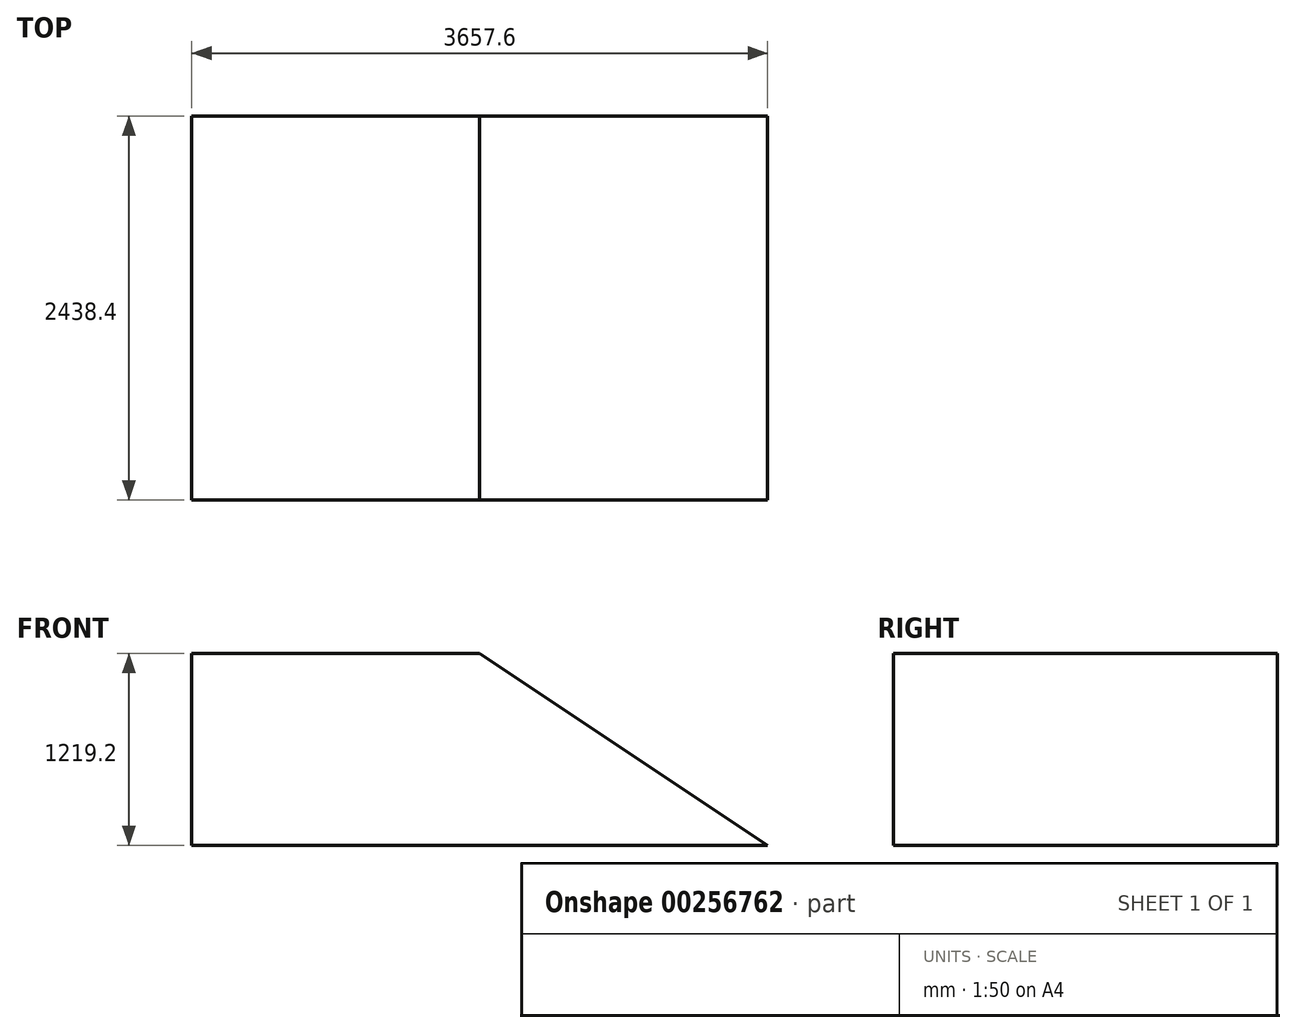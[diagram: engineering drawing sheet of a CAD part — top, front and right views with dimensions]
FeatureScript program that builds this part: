
annotation { "Feature Type Name" : "Feature", "Feature Type Description" : "" }
export const myFeature = defineFeature(function(context is Context, id is Id, definition is map)
    precondition{}
    {
        {
            var Q0;
            Q0=qCreatedBy(makeId("Front.planeOp"),FACE);
            var sketch = newSketch(context, id + "F0", { "sketchPlane" : qUnion([Q0])});
            skLineSegment(sketch, "E0.bottom", {"start": v(0, 0) * mm, "end": v(1828.8, 0) * mm});
            skLineSegment(sketch, "E0.top", {"start": v(0, 1219.2) * mm, "end": v(1828.8, 1219.2) * mm});
            skLineSegment(sketch, "E0.left", {"start": v(0, 0) * mm, "end": v(0, 1219.2) * mm});
            skLineSegment(sketch, "E0.right", {"start": v(1828.8, 0) * mm, "end": v(1828.8, 1219.2) * mm});
            skLineSegment(sketch, "E1", {"start": v(1828.8, 0) * mm, "end": v(3657.6, 0) * mm});
            skLineSegment(sketch, "E2", {"start": v(1828.8, 1219.2) * mm, "end": v(3657.6, 0) * mm});
            skSolve(sketch);
        }
        {
            var Q0;
            Q0=makeQuery(id+"F0.imprint","IMPRINT",FACE,{"disambiguationData":[TD([[makeQuery(id+"F0.imprint","IMPRINT",EDGE,{"derivedFrom":sQuery(id+"F0.wireOp",EDGE,"E0.left")}),1.0]])]});
            var Q1;
            Q1=makeQuery(id+"F0.imprint","IMPRINT",FACE,{"disambiguationData":[TD([[makeQuery(id+"F0.imprint","IMPRINT",EDGE,{"derivedFrom":sQuery(id+"F0.wireOp",EDGE,"E0.bottom")}),1.0]])]});
            var Q2;
            Q2=makeQuery(id+"F0.imprint","IMPRINT",FACE,{"disambiguationData":[TD([[makeQuery(id+"F0.imprint","IMPRINT",EDGE,{"derivedFrom":sQuery(id+"F0.wireOp",EDGE,"E0.right")}),-1.0]])]});
            var Q3;
            {var subQ0=sQuery(id+"F0.wireOp",EDGE,"XcISNvbV-igR6-hXD8-4gkA-qrv59Tn65qzj");Q3=makeQuery(id+"F0.imprint","IMPRINT",FACE,{"disambiguationData":[TD([[makeQuery(id+"F0.imprint","IMPRINT",EDGE,{"derivedFrom":subQ0}),-1.0]])]});}
            var Q4;
            {var subQ1=sQuery(id+"F0.wireOp",EDGE,"E0.top");var subQ3=sQuery(id+"F0.wireOp",EDGE,"B2NL7lis-7RjI-7pxC-DLYM-zCCmizm6cvdw");var subQ4=makeQuery(id+"F0.imprint","INTERSECT",VERTEX,{"derivedFrom":[subQ1,subQ3]});Q4=makeQuery(id+"F0.imprint","IMPRINT",FACE,{"disambiguationData":[TD([[makeQuery(id+"F0.imprint","IMPRINT",EDGE,{"disambiguationData":[TD([[subQ4,1.0]])],"derivedFrom":subQ3}),1.0]])]});}
            var Q5;
            {var subQ1=sQuery(id+"F0.wireOp",EDGE,"E0.top");var subQ3=sQuery(id+"F0.wireOp",EDGE,"B2NL7lis-7RjI-7pxC-DLYM-zCCmizm6cvdw");var subQ4=makeQuery(id+"F0.imprint","INTERSECT",VERTEX,{"derivedFrom":[subQ1,subQ3]});Q5=makeQuery(id+"F0.imprint","IMPRINT",FACE,{"disambiguationData":[TD([[makeQuery(id+"F0.imprint","IMPRINT",EDGE,{"disambiguationData":[TD([[subQ4,-1.0]])],"derivedFrom":subQ3}),1.0]])]});}
            extrude(context, id + "F1", {"entities" : qUnion([Q0, Q1, Q2, Q3, Q4, Q5]), "oppositeDirection" : true, "depth" : 2438.4 * mm, "symmetric" : true});
        }
    });
